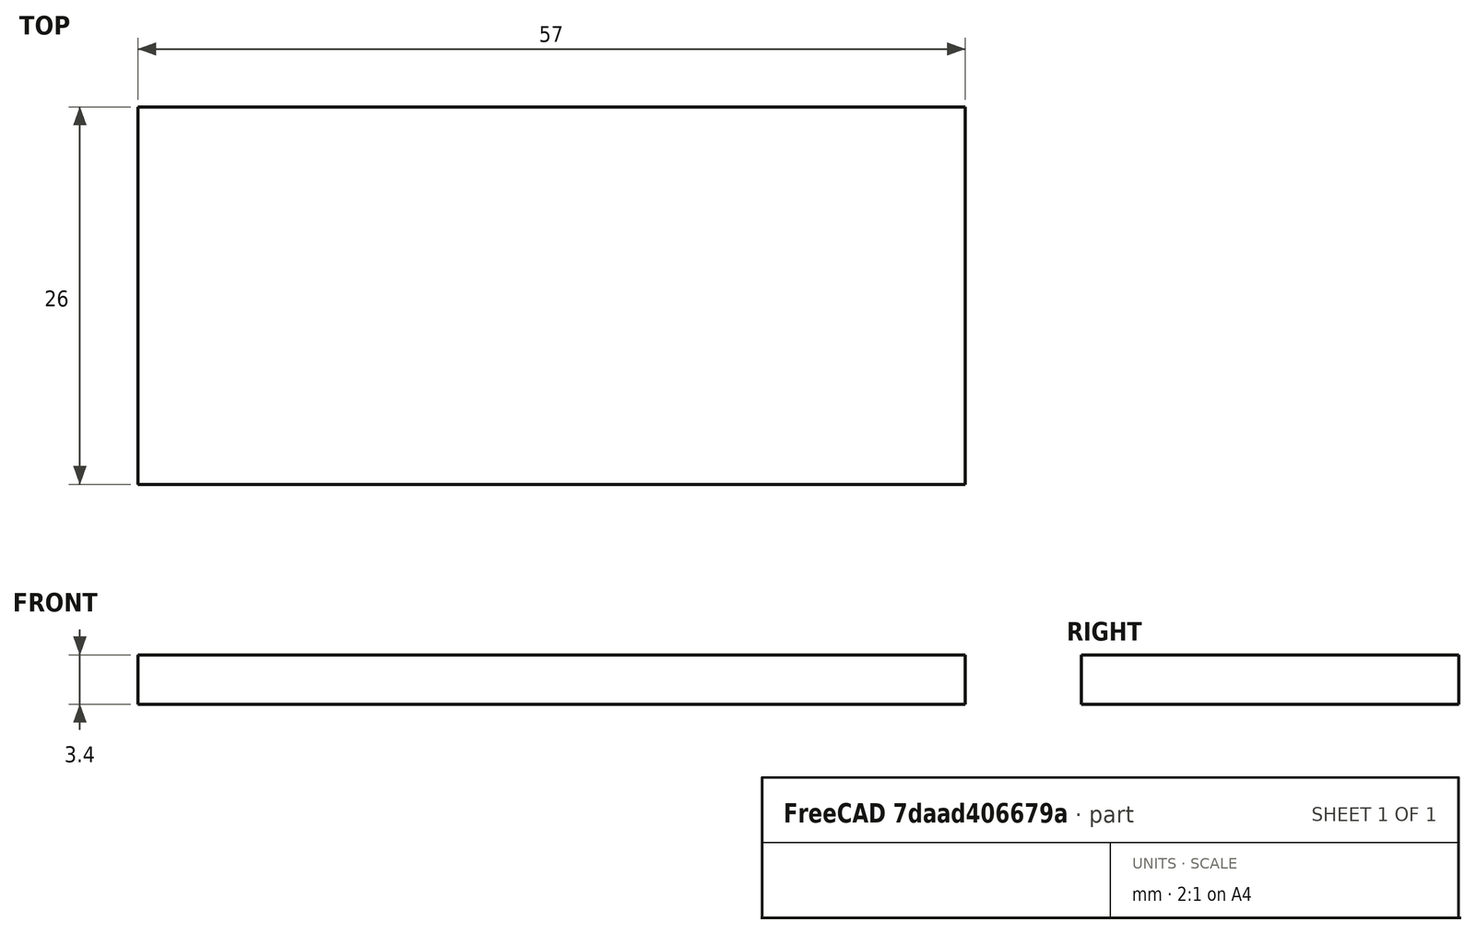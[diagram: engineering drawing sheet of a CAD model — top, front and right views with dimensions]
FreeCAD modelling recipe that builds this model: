
FCSTD DOCUMENT  (FreeCAD 0.17R12703 (Git))
Label: Servotraeger_oben
License: All rights reserved
LicenseURL: http://en.wikipedia.org/wiki/All_rights_reserved
objects: Path::FeaturePython×7, Part::FeaturePython×2, Part::Feature×1, App::FeaturePython×1, Path::FeatureCompoundPython×1
note: 5 computed .brp shape members not serialized (recipe doc carries the construction recipe); baked Part::Feature solids carry a one-line shape summary decoded from their .brp

FEATURE [Part::Feature] Part__Feature  label="Servotraeger_oben"
  Placement = pos=(0,0,-3.4) rot=(0,0,1;0rad)
  shape: bbox 57 x 26 x 3.4 mm, 26 faces (baked)
FEATURE [App::FeaturePython] SetupSheet  # Path/CAM operation (typed FeaturePython)
  ClearanceHeightExpression = StartDepth+SetupSheet.ClearanceHeightOffset
  ClearanceHeightOffset = 5
  FinalDepthExpression = OpFinalDepth
  HorizRapid = 0
  SafeHeightExpression = StartDepth+SetupSheet.SafeHeightOffset
  SafeHeightOffset = 3
  StartDepthExpression = OpStartDepth
  StepDownExpression = OpToolDiameter
  VertRapid = 0
FEATURE [Part::FeaturePython] Clone  label="Base-Servotraeger_oben"  # Draft clone (typed FeaturePython)
  AttacherType = Attacher::AttachEngine3D
  Fuse = false
  Objects = -> [Part__Feature]
  PathResource = Base
  Placement = pos=(0,0,-3.4) rot=(0,0,1;0rad)
  Scale = (1,1,1)
FEATURE [Part::FeaturePython] Stock  # WARN: FeaturePython — macro-defined, semantics opaque (R4)
  Base = -> Part__Feature
  ExtXneg = 0
  ExtXpos = 0
  ExtYneg = 0
  ExtYpos = 0
  ExtZneg = 0
  ExtZpos = 0
  StockType = FromBase
FEATURE [Path::FeaturePython] T1__Schaftfraeser_D2  label="T1: Schaftfraeser_D2"  # Path/CAM operation (typed FeaturePython)
  HorizFeed = 400
  HorizRapid = 0
  SpindleDir = 0
  SpindleSpeed = 0
  ToolNumber = 1
  VertFeed = 100
  VertRapid = 0
  expr: HorizRapid = SetupSheet.HorizRapid
  expr: VertRapid = SetupSheet.VertRapid
FEATURE [Path::FeaturePython] Profile_Faces  # Path/CAM operation (typed FeaturePython)
  Active = true
  AreaParams:
    OpenMode = 0
    Angle = 45.0
    MinArcPoints = 4
    Coplanar = 0
    Tolerance = 1e-07
    CleanDistance = 0.0
    PocketExtraOffset = 0.0
    AngleShift = 0.0
    SubjectFill = 0
    RoundPreceision = 0.0
    Simplify = False
    SectionTolerance = 1e-06
    MaxArcPoints = 100
    SectionOffset = 0.0
    Offset = -1.0
    Accuracy = 0.01
    PocketStepover = 0.0
    ClipFill = 0
    ToolRadius = 1.0
    Outline = False
    ClipperScale = 10000000.0
    FromCenter = False
    Explode = False
    EndType = 0
    Shift = 0.0
    ExtraPass = 0
    Project = False
    JoinType = 0
    Thicken = False
    Stepdown = 1.0
    SectionMode = 2
    MiterLimit = 2.0
    Deflection = 0.01
    Reorient = True
    FitArcs = True
    SectionCount = -1
    PocketMode = 0
    Stepover = 0.0
    Unit = 1.0
    Fill = 0
  Base = -> [Clone]
  ClearanceHeight = 5
  Direction = 0
  FinalDepth = -3.7
  JoinType = 0
  MiterLimit = 0.1
  OffsetExtra = 0
  OpFinalDepth = -3.4
  OpStartDepth = 0
  OpToolDiameter = 2
  PathParams = {'resume_height': 3.0, 'feedrate': 400.0, 'verbose': True, 'orientation': 1, 'return_end': True, 'preamble': False, 'retraction': 5.0, 'feedrate_v': 100.0}
  SafeHeight = 3
  Side = 1
  StartDepth = 0
  StartPoint = (0,0,0)
  StepDown = 2
  ToolController = -> T1__Schaftfraeser_D2
  UseComp = true
  UseStartPoint = false
  processCircles = false
  processHoles = false
  processPerimeter = true
  expr: ClearanceHeight = StartDepth + SetupSheet.ClearanceHeightOffset
  expr: SafeHeight = StartDepth + SetupSheet.SafeHeightOffset
  expr: StepDown = 2
  expr: FinalDepth = -3.7000000000000002
  expr: StartDepth = OpStartDepth
FEATURE [Path::FeaturePython] Contour  # Path/CAM operation (typed FeaturePython)
  Active = true
  AreaParams:
    OpenMode = 0
    Angle = 45.0
    MinArcPoints = 4
    Coplanar = 2
    Tolerance = 1e-07
    CleanDistance = 0.0
    PocketExtraOffset = 0.0
    AngleShift = 0.0
    SubjectFill = 0
    RoundPreceision = 0.0
    Simplify = False
    SectionTolerance = 1e-06
    MaxArcPoints = 100
    SectionOffset = 0.0
    Offset = 1.0
    Accuracy = 0.01
    PocketStepover = 0.0
    ClipFill = 0
    ToolRadius = 1.0
    Outline = False
    ClipperScale = 10000000.0
    FromCenter = False
    Explode = False
    EndType = 0
    Shift = 0.0
    ExtraPass = 0
    Project = False
    JoinType = 0
    Thicken = False
    Stepdown = 1.0
    SectionMode = 2
    MiterLimit = 2.0
    Deflection = 0.01
    Reorient = True
    FitArcs = True
    SectionCount = -1
    PocketMode = 0
    Stepover = 0.0
    Unit = 1.0
    Fill = 0
  ClearanceHeight = 5
  Direction = 1
  FinalDepth = -3.7
  JoinType = 0
  MiterLimit = 0.1
  OffsetExtra = 0
  OpFinalDepth = -3.4
  OpStartDepth = 0
  OpToolDiameter = 2
  PathParams = {'resume_height': 3.0, 'feedrate': 400.0, 'verbose': True, 'orientation': 0, 'return_end': True, 'preamble': False, 'retraction': 5.0, 'feedrate_v': 100.0}
  SafeHeight = 3
  Side = 0
  StartDepth = 0
  StartPoint = (0,0,0)
  StepDown = 2
  ToolController = -> T1__Schaftfraeser_D2
  UseComp = true
  UseStartPoint = false
  expr: ClearanceHeight = StartDepth + SetupSheet.ClearanceHeightOffset
  expr: SafeHeight = StartDepth + SetupSheet.SafeHeightOffset
  expr: StepDown = 2
  expr: FinalDepth = -3.7000000000000002
  expr: StartDepth = OpStartDepth
FEATURE [Path::FeaturePython] DogboneDressup  # Path/CAM operation (typed FeaturePython)
  Base = -> Profile_Faces
  Custom = 0
  Incision = 0
  Side = 0
  Style = 0
  ToolController = -> T1__Schaftfraeser_D2
FEATURE [Path::FeaturePython] DogboneDressup001  # Path/CAM operation (typed FeaturePython)
  Base = -> Contour
  Custom = 0
  Incision = 0
  Side = 0
  Style = 0
  ToolController = -> T1__Schaftfraeser_D2
FEATURE [Path::FeaturePython] TagDressup  # Path/CAM operation (typed FeaturePython)
  Angle = 45
  Base = -> DogboneDressup001
  Height = 1.6
  Positions = (3) [(28.5,27,0),(42,-1,0),(14.8,-1,0)]
  Radius = 0
  SegmentationFactor = 50
  Width = 4
FEATURE [Path::FeatureCompoundPython] Operations  # Path/CAM operation (typed FeaturePython)
  Group = -> [DogboneDressup,TagDressup]
  UsePlacements = false
FEATURE [Path::FeaturePython] Job  # Path/CAM operation (typed FeaturePython)
  Base = -> Clone
  GeometryTolerance = 0.01
  Operations = -> Operations
  PostProcessor = 5
  SetupSheet = -> SetupSheet
  Stock = -> Stock
  ToolController = -> [T1__Schaftfraeser_D2]
